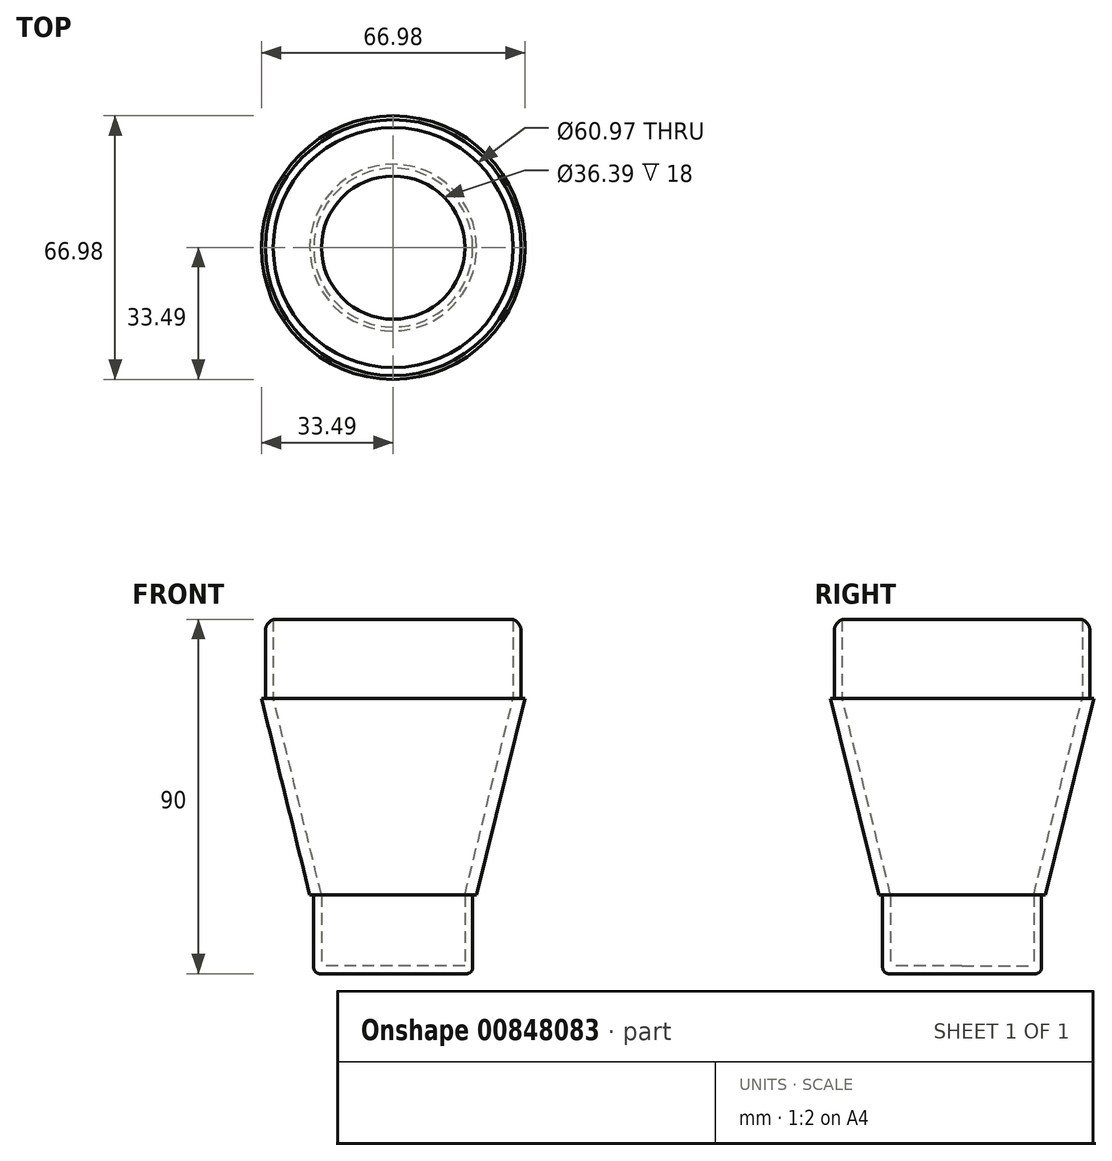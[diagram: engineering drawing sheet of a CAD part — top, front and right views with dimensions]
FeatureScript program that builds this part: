
annotation { "Feature Type Name" : "Feature", "Feature Type Description" : "" }
export const myFeature = defineFeature(function(context is Context, id is Id, definition is map)
    precondition{}
    {
        {
            var Q0;
            Q0=qCreatedBy(makeId("Front.planeOp"),FACE);
            var sketch = newSketch(context, id + "F0", { "sketchPlane" : qUnion([Q0])});
            skLineSegment(sketch, "E0", {"start": v(0, 0) * mm, "end": v(0, 24.56) * mm, "construction": true});
            skLineSegment(sketch, "E1", {"start": v(18.2, 0) * mm, "end": v(20.2, 0) * mm});
            skLineSegment(sketch, "E2", {"start": v(20.2, 0) * mm, "end": v(20.2, 20) * mm});
            skLineSegment(sketch, "E3", {"start": v(20.2, 20) * mm, "end": v(18.2, 20) * mm});
            skLineSegment(sketch, "E4", {"start": v(18.2, 20) * mm, "end": v(18.2, 0) * mm});
            skLineSegment(sketch, "E5", {"start": v(18.2, 20) * mm, "end": v(30.49, 70) * mm});
            skLineSegment(sketch, "E6", {"start": v(18.2, 20) * mm, "end": v(21.2, 20) * mm});
            skLineSegment(sketch, "E7", {"start": v(21.2, 20) * mm, "end": v(33.49, 70) * mm});
            skLineSegment(sketch, "E8", {"start": v(33.49, 70) * mm, "end": v(30.49, 70) * mm});
            skLineSegment(sketch, "E9", {"start": v(30.49, 70) * mm, "end": v(30.49, 90) * mm});
            skLineSegment(sketch, "E10", {"start": v(30.49, 90) * mm, "end": v(32.49, 90) * mm});
            skLineSegment(sketch, "E11", {"start": v(32.49, 90) * mm, "end": v(32.49, 70) * mm});
            skSolve(sketch);
        }
        {
            var Q0;
            Q0=makeQuery(id+"F0.imprint","IMPRINT",FACE,{"disambiguationData":[TD([[makeQuery(id+"F0.imprint","IMPRINT",EDGE,{"derivedFrom":sQuery(id+"F0.wireOp",EDGE,"E1")}),1.0]])]});
            var Q1;
            {var subQ3=sQuery(id+"F0.wireOp",EDGE,"E5");Q1=makeQuery(id+"F0.imprint","IMPRINT",FACE,{"disambiguationData":[TD([[makeQuery(id+"F0.imprint","IMPRINT",EDGE,{"derivedFrom":subQ3}),-1.0]])]});}
            var Q2;
            {var subQ0=sQuery(id+"F0.wireOp",EDGE,"E9");Q2=makeQuery(id+"F0.imprint","IMPRINT",FACE,{"disambiguationData":[TD([[makeQuery(id+"F0.imprint","IMPRINT",EDGE,{"derivedFrom":subQ0}),-1.0]])]});}
            var Q3;
            Q3=sQuery(id+"F0.wireOp",EDGE,"E0");
            revolve(context, id + "F1", {"surfaceOperationType" : NewSurfaceOperationType.NEW, "entities" : qUnion([Q0, Q1, Q2]), "axis" : qUnion([Q3]), "revolveType" : RevolveType.FULL});
        }
        {
            var Q0;
            Q0=qCreatedBy(makeId("Top.planeOp"),FACE);
            var sketch = newSketch(context, id + "F2", { "sketchPlane" : qUnion([Q0])});
            skCircle(sketch, "E12.0", {"center": v(0, 0) * mm, "radius": 18.2 * mm});
            skSolve(sketch);
        }
        {
            var Q0;
            Q0 = qSketchRegion(id + "F2", true);
            extrude(context, id + "F3", {"entities" : qUnion([Q0]), "operationType" : NewBodyOperationType.ADD, "depth" : 2 * mm, "offsetDistance" : 25.4 * mm});
        }
        {
            var Q0;
            Q0=makeQuery(id+"F1.opRevolve","SWEPT_EDGE",EDGE,{"disambiguationData":[OSD([sQuery(id+"F0.wireOp",EDGE,"E1"),sQuery(id+"F0.wireOp",EDGE,"E2")])]});
            fillet(context, id + "F4", {"entities" : qUnion([Q0]), "radius" : 1.59 * mm, "tangentPropagation" : true, "allowEdgeOverflow" : false});
        }
        {
            var Q0;
            Q0=makeQuery(id+"F1.opRevolve","SWEPT_EDGE",EDGE,{"disambiguationData":[OSD([sQuery(id+"F0.wireOp",EDGE,"E10"),sQuery(id+"F0.wireOp",EDGE,"E11")])]});
            fillet(context, id + "F5", {"entities" : qUnion([Q0]), "radius" : 3.17 * mm, "tangentPropagation" : true, "allowEdgeOverflow" : false});
        }
    });
